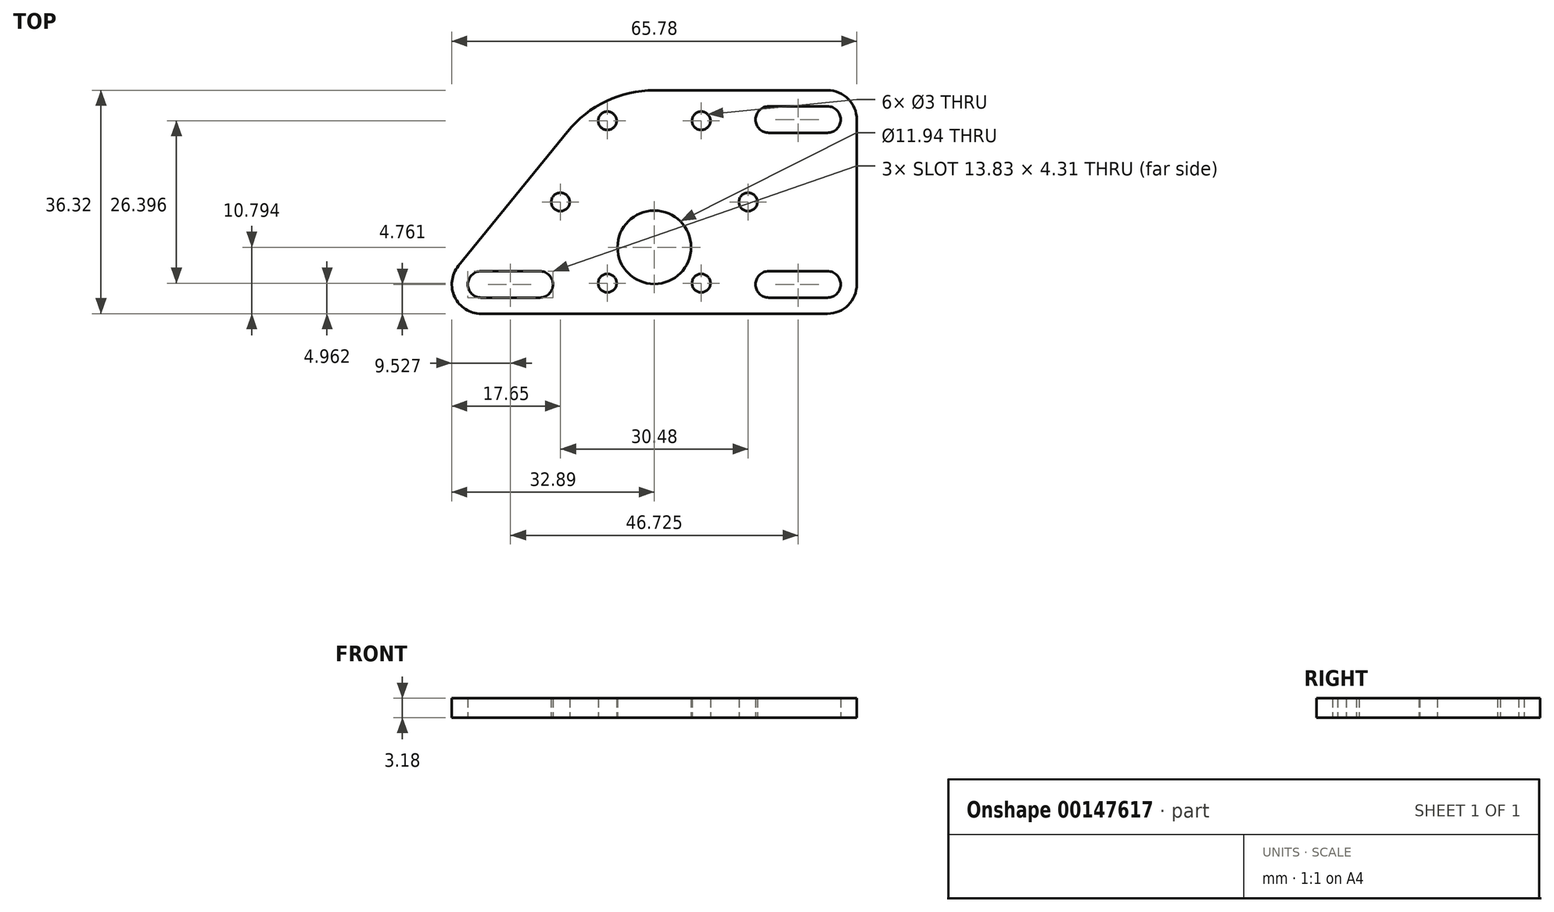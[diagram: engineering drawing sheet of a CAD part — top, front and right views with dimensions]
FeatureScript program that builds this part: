
annotation { "Feature Type Name" : "Feature", "Feature Type Description" : "" }
export const myFeature = defineFeature(function(context is Context, id is Id, definition is map)
    precondition{}
    {
        {
            var Q0;
            Q0=qCreatedBy(makeId("Top.planeOp"),FACE);
            var sketch = newSketch(context, id + "F0", { "sketchPlane" : qUnion([Q0])});
            skPoint(sketch, "E0.rect.middle", {"position": v(0, 0) * mm});
            skLineSegment(sketch, "E1", {"start": v(0, -7.37) * mm, "end": v(0, 7.37) * mm, "construction": true});
            skCircle(sketch, "E2.cCircle", {"center": v(0, 0) * mm, "radius": 13.2 * mm, "construction": true});
            skLineSegment(sketch, "E2.0", {"start": v(7.62, 13.2) * mm, "end": v(15.24, 0) * mm, "construction": true});
            skLineSegment(sketch, "E2.1", {"start": v(15.24, 0) * mm, "end": v(7.62, -13.2) * mm, "construction": true});
            skLineSegment(sketch, "E2.2", {"start": v(7.62, -13.2) * mm, "end": v(-7.62, -13.2) * mm, "construction": true});
            skLineSegment(sketch, "E2.3", {"start": v(-7.62, -13.2) * mm, "end": v(-15.24, 0) * mm, "construction": true});
            skLineSegment(sketch, "E2.4", {"start": v(-15.24, 0) * mm, "end": v(-7.62, 13.2) * mm, "construction": true});
            skLineSegment(sketch, "E2.5", {"start": v(-7.62, 13.2) * mm, "end": v(7.62, 13.2) * mm, "construction": true});
            skCircle(sketch, "E3", {"center": v(-7.62, 13.2) * mm, "radius": 1.5 * mm});
            skCircle(sketch, "E4", {"center": v(7.62, 13.2) * mm, "radius": 1.5 * mm});
            skCircle(sketch, "E5", {"center": v(15.24, 0) * mm, "radius": 1.5 * mm});
            skCircle(sketch, "E6", {"center": v(7.62, -13.2) * mm, "radius": 1.5 * mm});
            skCircle(sketch, "E7", {"center": v(-7.62, -13.2) * mm, "radius": 1.5 * mm});
            skCircle(sketch, "E8", {"center": v(-15.24, 0) * mm, "radius": 1.5 * mm});
            skArc(sketch, "E9", {"start": v(0, 18.16) * mm, "mid": v(-7.81, 16.4) * mm, "end": v(-14.1, 11.44) * mm});
            skCircle(sketch, "E10", {"center": v(-7.62, 13.2) * mm, "radius": 2.92 * mm, "construction": true});
            skArc(sketch, "E11", {"start": v(-31.82, -10.4) * mm, "mid": v(-32.42, -15.45) * mm, "end": v(-28.13, -18.16) * mm});
            skArc(sketch, "E12", {"start": v(-14.1, 11.44) * mm, "mid": v(7.81, -16.4) * mm, "end": v(0, 18.16) * mm, "construction": true});
            skLineSegment(sketch, "E13", {"start": v(-14.1, 11.44) * mm, "end": v(-31.82, -10.4) * mm});
            skLineSegment(sketch, "E14", {"start": v(-28.13, -18.16) * mm, "end": v(28.13, -18.16) * mm});
            skLineSegment(sketch, "E15", {"start": v(0, 18.16) * mm, "end": v(28.13, 18.16) * mm});
            skArc(sketch, "E16", {"start": v(28.13, -18.16) * mm, "mid": v(31.5, -16.77) * mm, "end": v(32.89, -13.4) * mm});
            skLineSegment(sketch, "E17", {"start": v(32.89, -13.4) * mm, "end": v(32.89, 13.4) * mm});
            skArc(sketch, "E18", {"start": v(32.89, 13.4) * mm, "mid": v(31.5, 16.77) * mm, "end": v(28.13, 18.16) * mm});
            skCircle(sketch, "E19", {"center": v(0, -7.37) * mm, "radius": 5.97 * mm});
            skLineSegment(sketch, "E20.bottom", {"start": v(28.13, -15.55) * mm, "end": v(18.6, -15.55) * mm});
            skLineSegment(sketch, "E20.top", {"start": v(28.13, -11.25) * mm, "end": v(18.6, -11.25) * mm});
            skLineSegment(sketch, "E20.left", {"start": v(28.13, -15.55) * mm, "end": v(28.13, -11.25) * mm});
            skLineSegment(sketch, "E20.right", {"start": v(18.6, -15.55) * mm, "end": v(18.6, -11.25) * mm});
            skLineSegment(sketch, "E21.bottom", {"start": v(28.13, 11.25) * mm, "end": v(18.6, 11.25) * mm});
            skLineSegment(sketch, "E21.top", {"start": v(28.13, 15.55) * mm, "end": v(18.6, 15.55) * mm});
            skLineSegment(sketch, "E21.left", {"start": v(28.13, 11.25) * mm, "end": v(28.13, 15.55) * mm, "construction": true});
            skLineSegment(sketch, "E21.right", {"start": v(18.6, 11.25) * mm, "end": v(18.6, 15.55) * mm, "construction": true});
            skArc(sketch, "E22", {"start": v(28.13, 11.25) * mm, "mid": v(30.28, 13.4) * mm, "end": v(28.13, 15.55) * mm});
            skArc(sketch, "E23", {"start": v(18.6, 15.55) * mm, "mid": v(16.45, 13.4) * mm, "end": v(18.6, 11.25) * mm});
            skCircle(sketch, "E24", {"center": v(18.6, 13.4) * mm, "radius": 4.76 * mm, "construction": true});
            skArc(sketch, "E25", {"start": v(18.6, -11.25) * mm, "mid": v(16.45, -13.4) * mm, "end": v(18.6, -15.55) * mm});
            skArc(sketch, "E26", {"start": v(28.13, -15.55) * mm, "mid": v(30.28, -13.4) * mm, "end": v(28.13, -11.25) * mm});
            skCircle(sketch, "E27", {"center": v(18.6, -13.4) * mm, "radius": 4.76 * mm, "construction": true});
            skLineSegment(sketch, "E28.bottom", {"start": v(-28.13, -11.25) * mm, "end": v(-18.6, -11.25) * mm});
            skLineSegment(sketch, "E28.top", {"start": v(-28.13, -15.55) * mm, "end": v(-18.6, -15.55) * mm});
            skLineSegment(sketch, "E28.left", {"start": v(-28.13, -11.25) * mm, "end": v(-28.13, -15.55) * mm});
            skLineSegment(sketch, "E28.right", {"start": v(-18.6, -11.25) * mm, "end": v(-18.6, -15.55) * mm});
            skArc(sketch, "E29", {"start": v(-18.6, -15.55) * mm, "mid": v(-16.45, -13.4) * mm, "end": v(-18.6, -11.25) * mm});
            skArc(sketch, "E30", {"start": v(-28.13, -11.25) * mm, "mid": v(-30.28, -13.4) * mm, "end": v(-28.13, -15.55) * mm});
            skCircle(sketch, "E31", {"center": v(-18.6, -13.4) * mm, "radius": 4.76 * mm, "construction": true});
            skSolve(sketch);
        }
        {
            var Q0;
            Q0=qSketchRegion(id+"F0",true);
            extrude(context, id + "F1", {"entities" : qUnion([Q0]), "depth" : 3.17 * mm});
        }
    });
